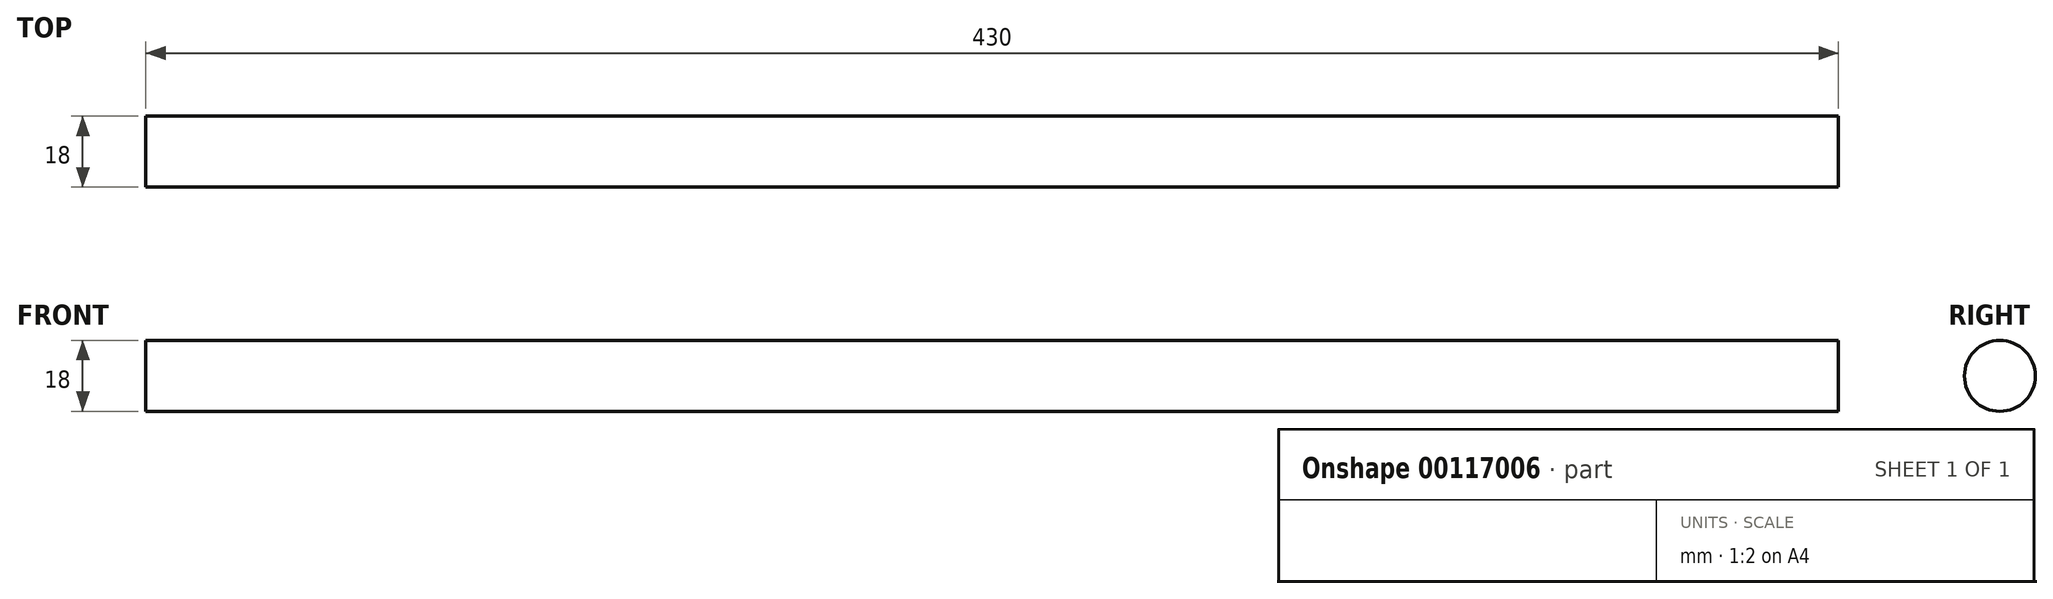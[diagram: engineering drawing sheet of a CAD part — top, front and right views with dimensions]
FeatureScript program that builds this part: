
annotation { "Feature Type Name" : "Feature", "Feature Type Description" : "" }
export const myFeature = defineFeature(function(context is Context, id is Id, definition is map)
    precondition{}
    {
        {
            var Q0;
            Q0=qCreatedBy(makeId("Right.planeOp"),FACE);
            var sketch = newSketch(context, id + "F0", { "sketchPlane" : qUnion([Q0])});
            skCircle(sketch, "E0", {"center": v(0, 0) * mm, "radius": 9 * mm});
            skSolve(sketch);
        }
        {
            var Q0;
            Q0=makeQuery(id+"F0.imprint","IMPRINT",FACE,{"disambiguationData":[TD([[makeQuery(id+"F0.imprint","IMPRINT",EDGE,{"derivedFrom":sQuery(id+"F0.wireOp",EDGE,"E0")}),1.0]])]});
            extrude(context, id + "F1", {"entities" : qUnion([Q0]), "depth" : (390 + 20 + 20) * mm, "offsetDistance" : 25 * mm});
        }
    });
